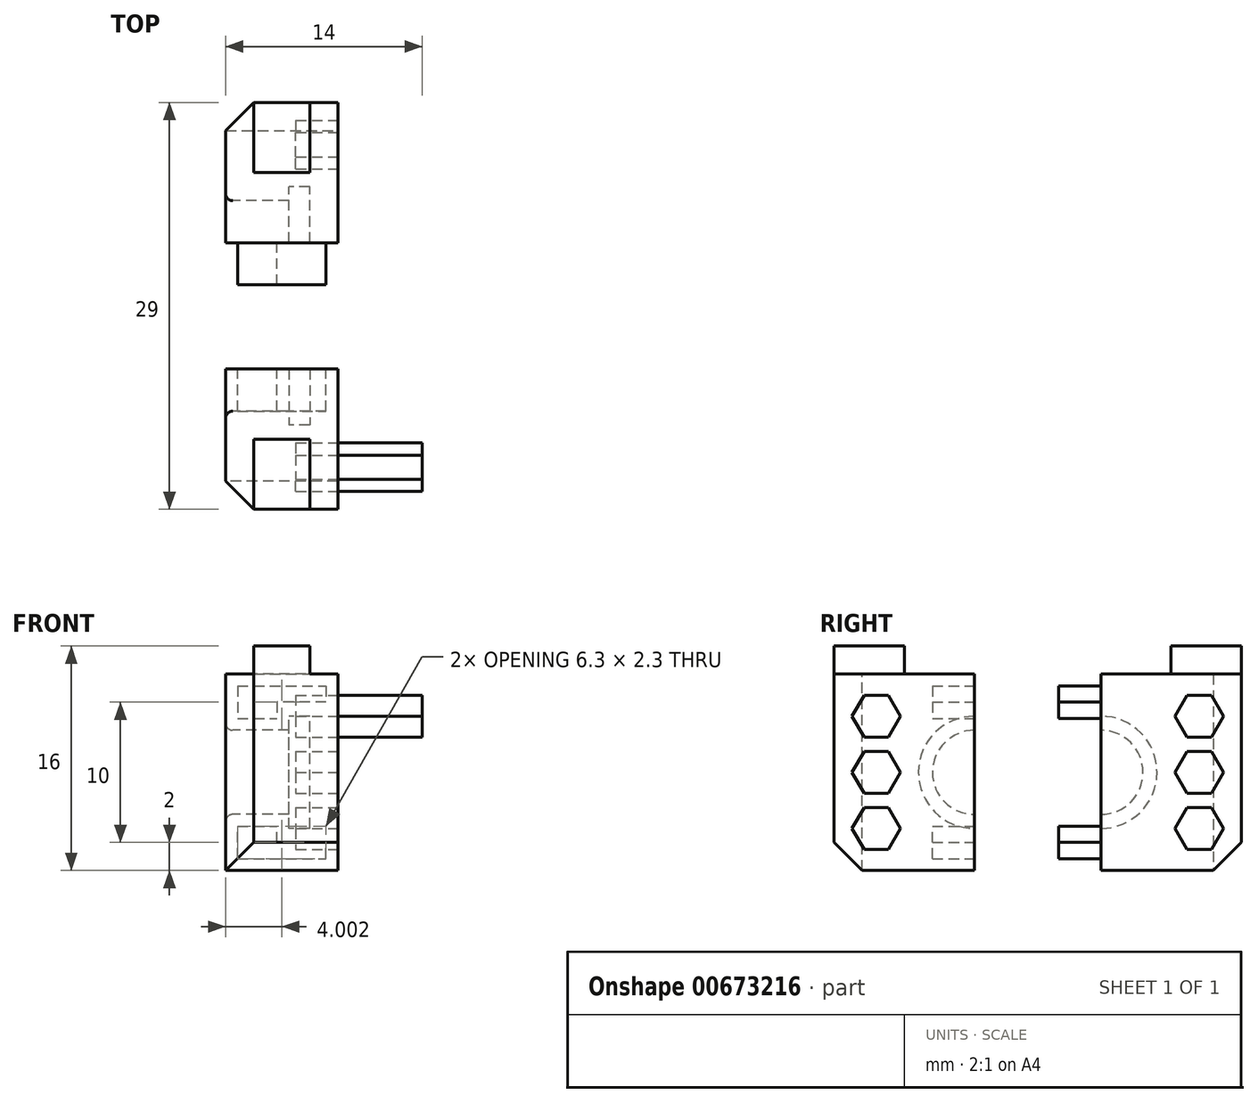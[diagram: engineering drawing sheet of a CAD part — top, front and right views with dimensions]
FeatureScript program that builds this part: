
annotation { "Feature Type Name" : "Feature", "Feature Type Description" : "" }
export const myFeature = defineFeature(function(context is Context, id is Id, definition is map)
    precondition{}
    {
        {
            var Q0;
            Q0=qCreatedBy(makeId("Right.planeOp"),FACE);
            var sketch = newSketch(context, id + "F0", { "sketchPlane" : qUnion([Q0])});
            skLineSegment(sketch, "E0.bottom", {"start": v(0, 0) * mm, "end": v(10, 0) * mm});
            skLineSegment(sketch, "E0.top", {"start": v(0, 14) * mm, "end": v(10, 14) * mm});
            skLineSegment(sketch, "E0.left", {"start": v(0, 0) * mm, "end": v(0, 14) * mm});
            skLineSegment(sketch, "E0.right", {"start": v(10, 0) * mm, "end": v(10, 14) * mm});
            skSolve(sketch);
        }
        {
            var Q0;
            Q0=qSketchRegion(id+"F0",true);
            extrude(context, id + "F1", {"entities" : qUnion([Q0]), "depth" : 8 * mm});
        }
        {
            var Q0;
            Q0=makeQuery(id+"F1.opExtrude","CAP_FACE",FACE,{"disambiguationData":[OSD([sQuery(id+"F0.wireOp",EDGE,"E0.bottom"),sQuery(id+"F0.wireOp",EDGE,"E0.top"),sQuery(id+"F0.wireOp",EDGE,"E0.left"),sQuery(id+"F0.wireOp",EDGE,"E0.right")])],"isStart":true});
            var sketch = newSketch(context, id + "F2", { "sketchPlane" : qUnion([Q0])});
            skArc(sketch, "E1", {"start": v(-10, 3) * mm, "mid": v(-6, 7) * mm, "end": v(-10, 11) * mm});
            skArc(sketch, "E2", {"start": v(-10, 4) * mm, "mid": v(-7, 7) * mm, "end": v(-10, 10) * mm});
            skLineSegment(sketch, "E3", {"start": v(-10, 11) * mm, "end": v(-10, 3) * mm});
            skSolve(sketch);
        }
        {
            var Q0;
            {var subQ0=sQuery(id+"F2.wireOp",EDGE,"E1");Q0=makeQuery(id+"F2.imprint","IMPRINT",FACE,{"disambiguationData":[TD([[makeQuery(id+"F2.imprint","IMPRINT",EDGE,{"derivedFrom":subQ0}),1.0]])]});}
            var Q1;
            {var subQ0=sQuery(id+"F2.wireOp",EDGE,"E2");Q1=makeQuery(id+"F2.imprint","IMPRINT",FACE,{"disambiguationData":[TD([[makeQuery(id+"F2.imprint","IMPRINT",EDGE,{"derivedFrom":subQ0}),1.0]])]});}
            extrude(context, id + "F3", {"entities" : qUnion([Q0, Q1]), "operationType" : NewBodyOperationType.REMOVE, "oppositeDirection" : true, "depth" : 6 * mm});
        }
        {
            var Q0;
            {var subQ0=sQuery(id+"F2.wireOp",EDGE,"E1");Q0=makeQuery(id+"F2.imprint","IMPRINT",FACE,{"disambiguationData":[TD([[makeQuery(id+"F2.imprint","IMPRINT",EDGE,{"derivedFrom":subQ0}),1.0]])]});}
            extrude(context, id + "F4", {"entities" : qUnion([Q0]), "operationType" : NewBodyOperationType.ADD, "oppositeDirection" : true, "depth" : 4.5 * mm});
        }
        {
            var Q0;
            {var subQ0=sQuery(id+"F2.wireOp",EDGE,"E3");var subQ2=sQuery(id+"F0.wireOp",EDGE,"E0.right");var subQ4=sQuery(id+"F2.wireOp",EDGE,"E2");Q0=makeQuery(id+"F4.boolean.opBoolean","MERGE",FACE,{"derivedFrom":[makeQuery(id+"F1.opExtrude","SWEPT_FACE",FACE,{"disambiguationData":[OSD([subQ2])]}),makeQuery(id+"F4.opExtrude","SWEPT_FACE",FACE,{"disambiguationData":[OSD([subQ0]),TDD([makeQuery(id+"F2.imprint","IMPRINT",EDGE,{"disambiguationData":[TD([[makeQuery(id+"F2.imprint","INTERSECT",VERTEX,{"disambiguationData":[OD(0.0)],"derivedFrom":[subQ4,subQ0]}),1.0]])],"derivedFrom":subQ0})])]}),makeQuery(id+"F4.opExtrude","SWEPT_FACE",FACE,{"disambiguationData":[OSD([subQ0]),TDD([makeQuery(id+"F2.imprint","IMPRINT",EDGE,{"disambiguationData":[TD([[makeQuery(id+"F2.imprint","INTERSECT",VERTEX,{"disambiguationData":[OD(1.0)],"derivedFrom":[subQ4,subQ0]}),-1.0]])],"derivedFrom":subQ0})])]})]});}
            var sketch = newSketch(context, id + "F5", { "sketchPlane" : qUnion([Q0])});
            skLineSegment(sketch, "E4.0", {"start": v(-0.85, 13.15) * mm, "end": v(-0.85, 10.85) * mm});
            skLineSegment(sketch, "E4.1", {"start": v(-0.85, 13.15) * mm, "end": v(-3.65, 13.15) * mm});
            skLineSegment(sketch, "E4.2", {"start": v(-3.65, 12) * mm, "end": v(-3.65, 10.85) * mm});
            skLineSegment(sketch, "E4.3", {"start": v(-0.85, 10.85) * mm, "end": v(-3.65, 10.85) * mm});
            skLineSegment(sketch, "E5", {"start": v(-8, 7) * mm, "end": v(-6, 7) * mm, "construction": true});
            skLineSegment(sketch, "E6.MirrorCS", {"start": v(-0.85, 0.85) * mm, "end": v(-0.85, 3.15) * mm});
            skLineSegment(sketch, "E7.MirrorCS", {"start": v(-3.65, 2) * mm, "end": v(-3.65, 3.15) * mm});
            skLineSegment(sketch, "E8.MirrorCS", {"start": v(-0.85, 0.85) * mm, "end": v(-3.65, 0.85) * mm});
            skLineSegment(sketch, "E9.MirrorCS", {"start": v(-0.85, 3.15) * mm, "end": v(-3.65, 3.15) * mm});
            skLineSegment(sketch, "E10", {"start": v(-3.65, 13.15) * mm, "end": v(-7.15, 13.15) * mm});
            skLineSegment(sketch, "E11", {"start": v(-7.15, 13.15) * mm, "end": v(-7.15, 12) * mm});
            skPoint(sketch, "E11.endSnap0", {"position": v(-3.65, 12) * mm});
            skLineSegment(sketch, "E12", {"start": v(-7.15, 12) * mm, "end": v(-3.65, 12) * mm});
            skLineSegment(sketch, "E13.MirrorCS", {"start": v(-3.65, 0.85) * mm, "end": v(-7.15, 0.85) * mm});
            skLineSegment(sketch, "E14.MirrorCS", {"start": v(-7.15, 2) * mm, "end": v(-3.65, 2) * mm});
            skLineSegment(sketch, "E15.MirrorCS", {"start": v(-7.15, 0.85) * mm, "end": v(-7.15, 2) * mm});
            skSolve(sketch);
        }
        {
            var Q0;
            Q0=qSketchRegion(id+"F5",true);
            extrude(context, id + "F6", {"entities" : qUnion([Q0]), "operationType" : NewBodyOperationType.REMOVE, "oppositeDirection" : true, "depth" : 3 * mm});
        }
        {
            var Q0;
            Q0=makeQuery(id+"F4.opExtrude","CAP_EDGE",EDGE,{"disambiguationData":[OSD([sQuery(id+"F2.wireOp",EDGE,"E2")])],"isStart":true});
            fillet(context, id + "F7", {"entities" : qUnion([Q0]), "radius" : .5 * mm, "tangentPropagation" : true, "allowEdgeOverflow" : false});
        }
        {
            var Q0;
            Q0=makeQuery(id+"F1.opExtrude","CAP_FACE",FACE,{"disambiguationData":[OSD([sQuery(id+"F0.wireOp",EDGE,"E0.bottom"),sQuery(id+"F0.wireOp",EDGE,"E0.top"),sQuery(id+"F0.wireOp",EDGE,"E0.left"),sQuery(id+"F0.wireOp",EDGE,"E0.right")])],"isStart":false});
            var sketch = newSketch(context, id + "F8", { "sketchPlane" : qUnion([Q0])});
            skCircle(sketch, "E16.cCircle", {"center": v(3, 11) * mm, "radius": 1.5 * mm, "construction": true});
            skLineSegment(sketch, "E16.0", {"start": v(3.87, 9.5) * mm, "end": v(2.13, 9.5) * mm});
            skLineSegment(sketch, "E16.1", {"start": v(2.13, 9.5) * mm, "end": v(1.27, 11) * mm});
            skLineSegment(sketch, "E16.2", {"start": v(1.27, 11) * mm, "end": v(2.13, 12.5) * mm});
            skLineSegment(sketch, "E16.3", {"start": v(2.13, 12.5) * mm, "end": v(3.87, 12.5) * mm});
            skLineSegment(sketch, "E16.4", {"start": v(3.87, 12.5) * mm, "end": v(4.73, 11) * mm});
            skLineSegment(sketch, "E16.5", {"start": v(4.73, 11) * mm, "end": v(3.87, 9.5) * mm});
            skPoint(sketch, "E16.0.midPoint", {"position": v(3, 9.5) * mm});
            skLineSegment(sketch, "E17", {"start": v(10, 7) * mm, "end": v(6.47, 7) * mm, "construction": true});
            skLineSegment(sketch, "E18.MirrorCS", {"start": v(3.87, 4.5) * mm, "end": v(2.13, 4.5) * mm});
            skLineSegment(sketch, "E19.MirrorCS", {"start": v(1.27, 3) * mm, "end": v(2.13, 1.5) * mm});
            skLineSegment(sketch, "E20.MirrorCS", {"start": v(2.13, 1.5) * mm, "end": v(3.87, 1.5) * mm});
            skPoint(sketch, "E21.MirrorP", {"position": v(3, 4.5) * mm});
            skCircle(sketch, "E22.MirrorC", {"center": v(3, 3) * mm, "radius": 1.5 * mm, "construction": true});
            skLineSegment(sketch, "E23.MirrorCS", {"start": v(2.13, 4.5) * mm, "end": v(1.27, 3) * mm});
            skLineSegment(sketch, "E24.MirrorCS", {"start": v(4.73, 3) * mm, "end": v(3.87, 4.5) * mm});
            skLineSegment(sketch, "E25.MirrorCS", {"start": v(3.87, 1.5) * mm, "end": v(4.73, 3) * mm});
            skCircle(sketch, "E26.cCircle", {"center": v(3, 7) * mm, "radius": 1.5 * mm, "construction": true});
            skLineSegment(sketch, "E26.0", {"start": v(3.87, 5.5) * mm, "end": v(2.13, 5.5) * mm});
            skLineSegment(sketch, "E26.1", {"start": v(2.13, 5.5) * mm, "end": v(1.27, 7) * mm});
            skLineSegment(sketch, "E26.2", {"start": v(1.27, 7) * mm, "end": v(2.13, 8.5) * mm});
            skLineSegment(sketch, "E26.3", {"start": v(2.13, 8.5) * mm, "end": v(3.87, 8.5) * mm});
            skLineSegment(sketch, "E26.4", {"start": v(3.87, 8.5) * mm, "end": v(4.73, 7) * mm});
            skLineSegment(sketch, "E26.5", {"start": v(4.73, 7) * mm, "end": v(3.87, 5.5) * mm});
            skPoint(sketch, "E26.0.midPoint", {"position": v(3, 5.5) * mm});
            skSolve(sketch);
        }
        {
            var Q0;
            Q0=qSketchRegion(id+"F8",true);
            extrude(context, id + "F9", {"entities" : qUnion([Q0]), "operationType" : NewBodyOperationType.REMOVE, "oppositeDirection" : true, "depth" : 3 * mm});
        }
        {
            var Q0;
            Q0=makeQuery(id+"F8.imprint","IMPRINT",FACE,{"disambiguationData":[TD([[makeQuery(id+"F8.imprint","IMPRINT",EDGE,{"derivedFrom":sQuery(id+"F8.wireOp",EDGE,"E16.0")}),-1.0]])]});
            extrude(context, id + "F10", {"entities" : qUnion([Q0]), "depth" : 6 * mm});
        }
        {
            var Q0;
            Q0=qCreatedBy(makeId("Front.planeOp"),FACE);
            cPlane(context, id + "F11", {"entities" : qUnion([Q0]), "cplaneType" : CPlaneType.OFFSET, "offset" : 14.5 * mm, "oppositeDirection" : true, "width" : 150 * mm, "height" : 150 * mm});
        }
        {
            var Q0;
            Q0=makeQuery(id+"F1.opExtrude","SWEPT_BODY",BODY,{"disambiguationData":[OSD([sQuery(id+"F0.wireOp",EDGE,"E0.bottom"),sQuery(id+"F0.wireOp",EDGE,"E0.top"),sQuery(id+"F0.wireOp",EDGE,"E0.left"),sQuery(id+"F0.wireOp",EDGE,"E0.right")])]});
            var Q1;
            Q1=qCreatedBy(id+"F11.planeOp",FACE);
            mirror(context, id + "F12", {"entities" : qUnion([Q0]), "mirrorPlane" : qUnion([Q1])});
        }
        {
            var Q0;
            Q0=makeQuery(id+"F12.opPattern","COPY",FACE,{"derivedFrom":makeQuery(id+"F6.boolean.opBoolean","COPY",FACE,{"derivedFrom":makeQuery(id+"F6.opExtrude","CAP_FACE",FACE,{"disambiguationData":[OSD([sQuery(id+"F5.wireOp",EDGE,"E4.0"),sQuery(id+"F5.wireOp",EDGE,"E4.1"),sQuery(id+"F5.wireOp",EDGE,"E4.2"),sQuery(id+"F5.wireOp",EDGE,"E4.3"),sQuery(id+"F5.wireOp",EDGE,"E10"),sQuery(id+"F5.wireOp",EDGE,"E11"),sQuery(id+"F5.wireOp",EDGE,"E12")])],"isStart":false})}),"instanceName":"1"});
            var Q1;
            Q1=makeQuery(id+"F12.opPattern","COPY",FACE,{"derivedFrom":makeQuery(id+"F6.boolean.opBoolean","COPY",FACE,{"derivedFrom":makeQuery(id+"F6.opExtrude","CAP_FACE",FACE,{"disambiguationData":[OSD([sQuery(id+"F5.wireOp",EDGE,"E6.MirrorCS"),sQuery(id+"F5.wireOp",EDGE,"E7.MirrorCS"),sQuery(id+"F5.wireOp",EDGE,"E8.MirrorCS"),sQuery(id+"F5.wireOp",EDGE,"E9.MirrorCS"),sQuery(id+"F5.wireOp",EDGE,"E13.MirrorCS"),sQuery(id+"F5.wireOp",EDGE,"E14.MirrorCS"),sQuery(id+"F5.wireOp",EDGE,"E15.MirrorCS")])],"isStart":false})}),"instanceName":"1"});
            extrude(context, id + "F13", {"entities" : qUnion([Q0, Q1]), "operationType" : NewBodyOperationType.ADD, "depth" : 6 * mm});
        }
        {
            var Q0;
            Q0=makeQuery(id+"F1.opExtrude","SWEPT_FACE",FACE,{"disambiguationData":[OSD([sQuery(id+"F0.wireOp",EDGE,"E0.top")])]});
            var sketch = newSketch(context, id + "F14", { "sketchPlane" : qUnion([Q0])});
            skLineSegment(sketch, "E27.bottom", {"start": v(8, 0) * mm, "end": v(6, 0) * mm, "construction": true});
            skLineSegment(sketch, "E27.top", {"start": v(8, 5) * mm, "end": v(6, 5) * mm, "construction": true});
            skLineSegment(sketch, "E27.left", {"start": v(8, 0) * mm, "end": v(8, 5) * mm, "construction": true});
            skLineSegment(sketch, "E27.right", {"start": v(6, 0) * mm, "end": v(6, 5) * mm, "construction": true});
            skPoint(sketch, "E28.oppositeSnap0", {"position": v(7, 5) * mm});
            skLineSegment(sketch, "E28.bottom", {"start": v(6, 0) * mm, "end": v(2, 0) * mm});
            skLineSegment(sketch, "E28.top", {"start": v(6, 5) * mm, "end": v(2, 5) * mm});
            skLineSegment(sketch, "E28.left", {"start": v(6, 0) * mm, "end": v(6, 5) * mm});
            skLineSegment(sketch, "E28.right", {"start": v(2, 0) * mm, "end": v(2, 5) * mm});
            skSolve(sketch);
        }
        {
            var Q0;
            Q0=qSketchRegion(id+"F14",true);
            extrude(context, id + "F15", {"entities" : qUnion([Q0]), "operationType" : NewBodyOperationType.ADD, "depth" : 2 * mm});
        }
        {
            var Q0;
            Q0=makeQuery(id+"F12.opPattern","COPY",FACE,{"derivedFrom":makeQuery(id+"F1.opExtrude","SWEPT_FACE",FACE,{"disambiguationData":[OSD([sQuery(id+"F0.wireOp",EDGE,"E0.top")])]}),"instanceName":"1"});
            var sketch = newSketch(context, id + "F16", { "sketchPlane" : qUnion([Q0])});
            skLineSegment(sketch, "E29", {"start": v(0, 29) * mm, "end": v(2, 29) * mm, "construction": true});
            skLineSegment(sketch, "E30.bottom", {"start": v(2, 29) * mm, "end": v(6, 29) * mm});
            skLineSegment(sketch, "E30.top", {"start": v(2, 24) * mm, "end": v(6, 24) * mm});
            skLineSegment(sketch, "E30.left", {"start": v(2, 29) * mm, "end": v(2, 24) * mm});
            skLineSegment(sketch, "E30.right", {"start": v(6, 29) * mm, "end": v(6, 24) * mm});
            skSolve(sketch);
        }
        {
            var Q0;
            Q0=qSketchRegion(id+"F16",true);
            extrude(context, id + "F17", {"entities" : qUnion([Q0]), "operationType" : NewBodyOperationType.ADD, "depth" : 2 * mm});
        }
        {
            var Q0;
            Q0=makeQuery(id+"F1.opExtrude","SWEPT_EDGE",EDGE,{"disambiguationData":[OSD([sQuery(id+"F0.wireOp",EDGE,"E0.bottom"),sQuery(id+"F0.wireOp",EDGE,"E0.left")])]});
            var Q1;
            Q1=makeQuery(id+"F12.opPattern","COPY",EDGE,{"derivedFrom":makeQuery(id+"F1.opExtrude","SWEPT_EDGE",EDGE,{"disambiguationData":[OSD([sQuery(id+"F0.wireOp",EDGE,"E0.bottom"),sQuery(id+"F0.wireOp",EDGE,"E0.left")])]}),"instanceName":"1"});
            var Q2;
            Q2=makeQuery(id+"F1.opExtrude","CAP_EDGE",EDGE,{"disambiguationData":[OSD([sQuery(id+"F0.wireOp",EDGE,"E0.left")])],"isStart":true});
            var Q3;
            Q3=makeQuery(id+"F12.opPattern","COPY",EDGE,{"derivedFrom":makeQuery(id+"F1.opExtrude","CAP_EDGE",EDGE,{"disambiguationData":[OSD([sQuery(id+"F0.wireOp",EDGE,"E0.left")])],"isStart":true}),"instanceName":"1"});
            chamfer(context, id + "F18", {"entities" : qUnion([Q0, Q1, Q2, Q3]), "width" : 2 * mm, "tangentPropagation" : true});
        }
    });
